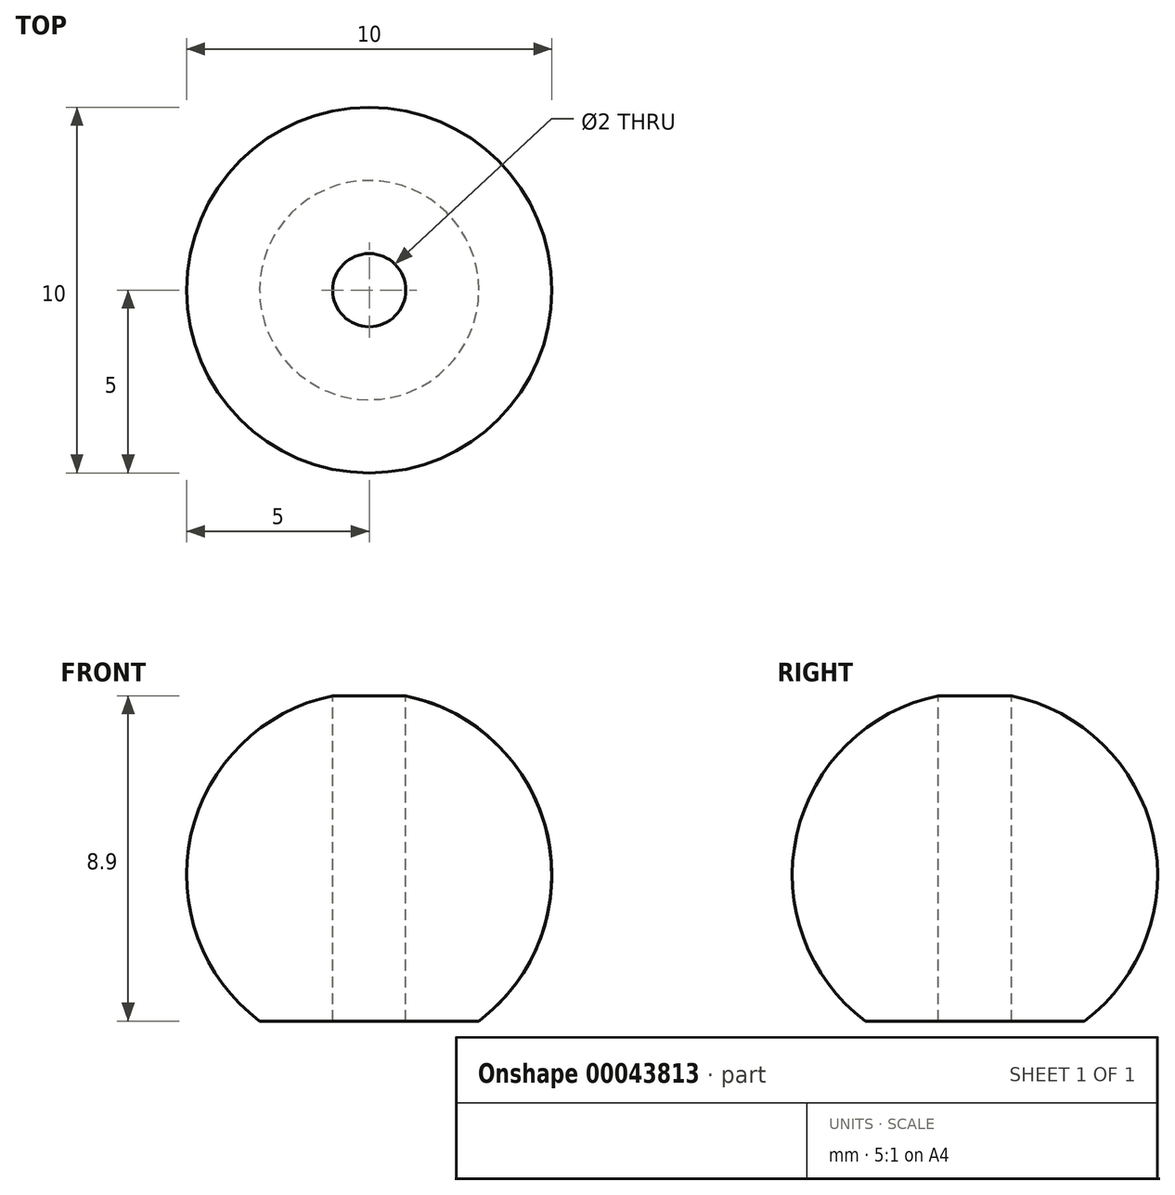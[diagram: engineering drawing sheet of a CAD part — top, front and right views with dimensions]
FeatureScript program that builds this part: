
annotation { "Feature Type Name" : "Feature", "Feature Type Description" : "" }
export const myFeature = defineFeature(function(context is Context, id is Id, definition is map)
    precondition{}
    {
        {
            var Q0;
            Q0=qCreatedBy(makeId("Front.planeOp"),FACE);
            var sketch = newSketch(context, id + "F0", { "sketchPlane" : qUnion([Q0])});
            skArc(sketch, "E0", {"start": v(-1, 4.9) * mm, "mid": v(-4.88, 1.1) * mm, "end": v(-3, -4) * mm});
            skLineSegment(sketch, "E1", {"start": v(0, 5) * mm, "end": v(0, -5) * mm, "construction": true});
            skLineSegment(sketch, "E2", {"start": v(-1, 4.9) * mm, "end": v(-1, -4) * mm});
            skLineSegment(sketch, "E3", {"start": v(-1, -4) * mm, "end": v(-3, -4) * mm});
            skSolve(sketch);
        }
        {
            var Q0;
            Q0 = qSketchRegion(id + "F0", true);
            var Q1;
            Q1=sQuery(id+"F0.wireOp",EDGE,"E1");
            revolve(context, id + "F1", {"entities" : qUnion([Q0]), "axis" : qUnion([Q1]), "revolveType" : RevolveType.FULL});
        }
    });
